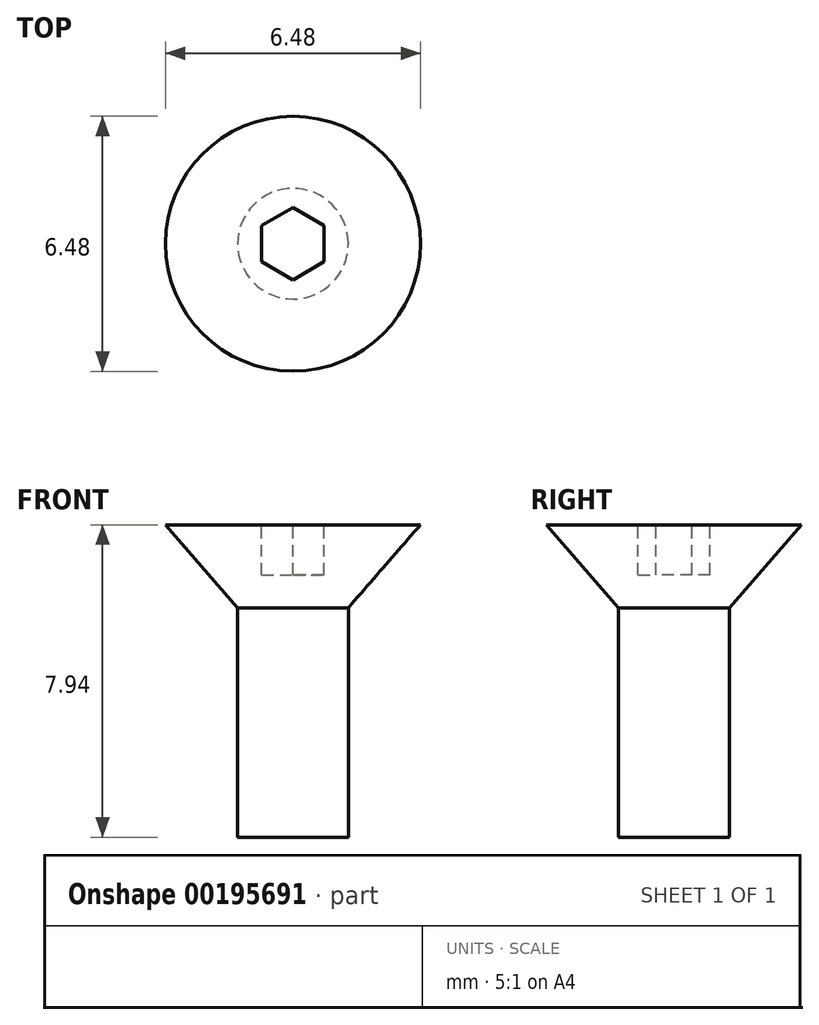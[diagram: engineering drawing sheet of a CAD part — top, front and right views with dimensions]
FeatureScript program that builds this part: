
annotation { "Feature Type Name" : "Feature", "Feature Type Description" : "" }
export const myFeature = defineFeature(function(context is Context, id is Id, definition is map)
    precondition{}
    {
        {
            var Q0;
            Q0=qCreatedBy(makeId("Top.planeOp"),FACE);
            var sketch = newSketch(context, id + "F0", { "sketchPlane" : qUnion([Q0])});
            skCircle(sketch, "E0", {"center": v(0, 0) * mm, "radius": 3.24 * mm});
            skSolve(sketch);
        }
        {
            var Q0;
            Q0 = qSketchRegion(id + "F0", true);
            extrude(context, id + "F1", {"entities" : qUnion([Q0]), "oppositeDirection" : true, "depth" : 2.1 * mm, "offsetDistance" : 25.4 * mm, "hasDraft" : true, "draftAngle" : 41 * degree, "draftPullDirection" : true});
        }
        {
            var Q0;
            Q0=makeQuery(id+"F1.opExtrude","CAP_FACE",FACE,{"disambiguationData":[OSD([sQuery(id+"F0.wireOp",EDGE,"E0")])],"isStart":true});
            cPlane(context, id + "F2", {"entities" : qUnion([Q0]), "cplaneType" : CPlaneType.OFFSET, "offset" : 7.94 * mm, "oppositeDirection" : true, "width" : 152.4 * mm, "height" : 152.4 * mm});
        }
        {
            var Q0;
            Q0=makeQuery(id+"F1.opExtrude","CAP_FACE",FACE,{"disambiguationData":[OSD([sQuery(id+"F0.wireOp",EDGE,"E0")])],"isStart":false});
            var Q1;
            Q1=qCreatedBy(id+"F2.planeOp",FACE);
            extrude(context, id + "F3", {"entities" : qUnion([Q0]), "operationType" : NewBodyOperationType.ADD, "endBound" : BoundingType.UP_TO_SURFACE, "depth" : 25.4 * mm, "endBoundEntityFace" : qUnion([Q1]), "offsetDistance" : 25.4 * mm});
        }
        {
            var Q0;
            Q0=makeQuery(id+"F1.opExtrude","CAP_FACE",FACE,{"disambiguationData":[OSD([sQuery(id+"F0.wireOp",EDGE,"E0")])],"isStart":true});
            var sketch = newSketch(context, id + "F4", { "sketchPlane" : qUnion([Q0])});
            skCircle(sketch, "E1.cCircle", {"center": v(0, 0) * mm, "radius": 0.8 * mm, "construction": true});
            skLineSegment(sketch, "E1.0", {"start": v(0.8, 0.46) * mm, "end": v(0.8, -0.46) * mm});
            skLineSegment(sketch, "E1.1", {"start": v(0.8, -0.46) * mm, "end": v(0, -0.92) * mm});
            skLineSegment(sketch, "E1.2", {"start": v(0, -0.92) * mm, "end": v(-0.8, -0.46) * mm});
            skLineSegment(sketch, "E1.3", {"start": v(-0.8, -0.46) * mm, "end": v(-0.8, 0.46) * mm});
            skLineSegment(sketch, "E1.4", {"start": v(-0.8, 0.46) * mm, "end": v(0, 0.92) * mm});
            skLineSegment(sketch, "E1.5", {"start": v(0, 0.92) * mm, "end": v(0.8, 0.46) * mm});
            skPoint(sketch, "E1.0.midPoint", {"position": v(0.8, 0) * mm});
            skSolve(sketch);
        }
        {
            var Q0;
            Q0 = qSketchRegion(id + "F4", true);
            extrude(context, id + "F5", {"entities" : qUnion([Q0]), "operationType" : NewBodyOperationType.REMOVE, "oppositeDirection" : true, "depth" : 1.27 * mm, "offsetDistance" : 25.4 * mm});
        }
    });
